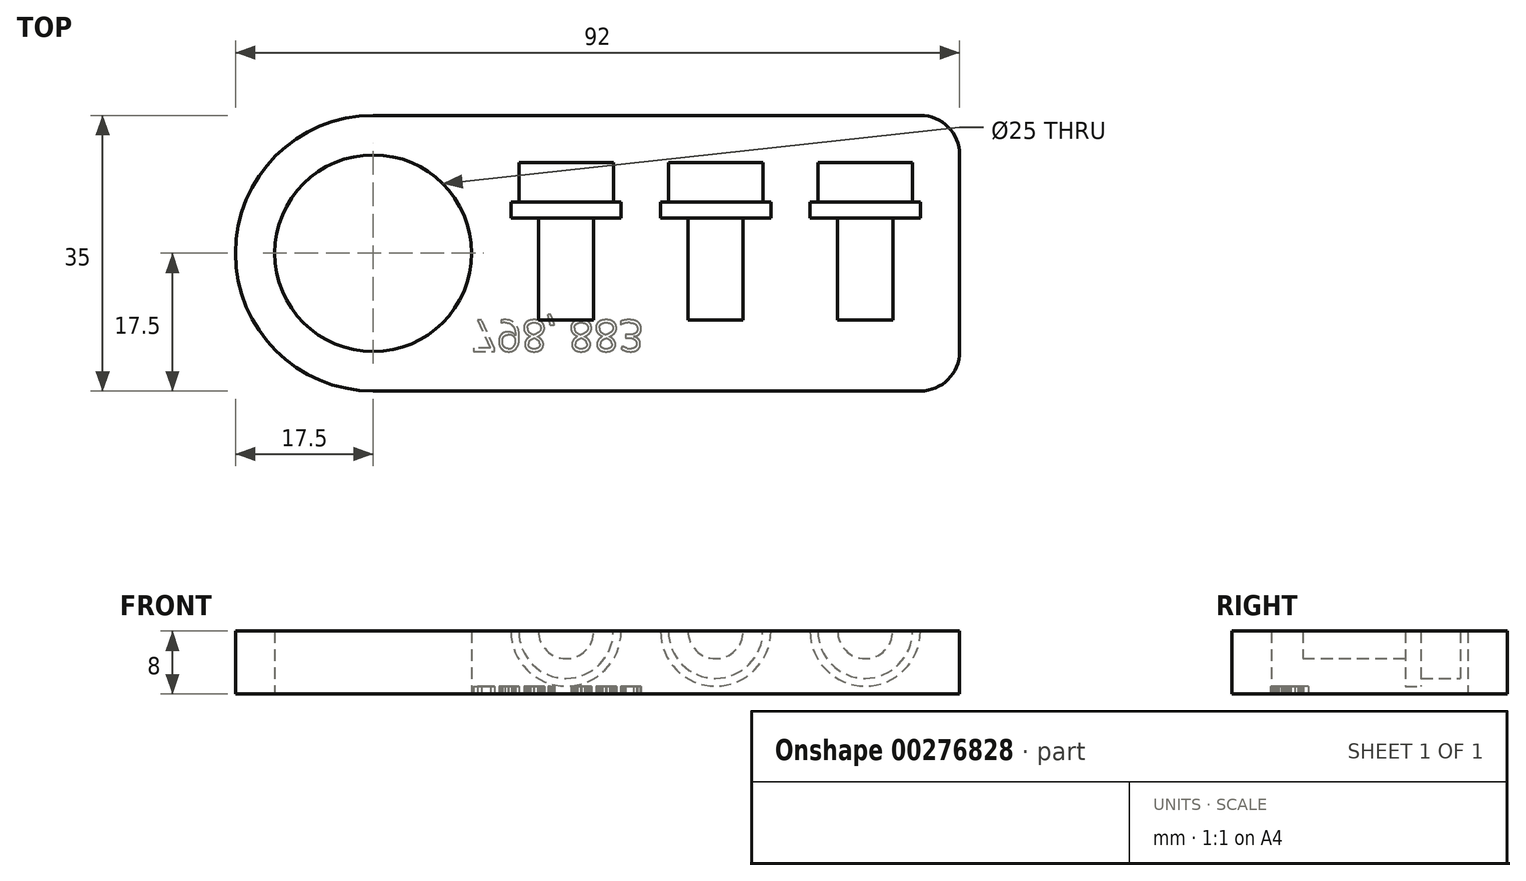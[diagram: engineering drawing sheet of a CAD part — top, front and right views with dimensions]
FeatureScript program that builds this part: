
annotation { "Feature Type Name" : "Feature", "Feature Type Description" : "" }
export const myFeature = defineFeature(function(context is Context, id is Id, definition is map)
    precondition{}
    {
        {
            var Q0;
            Q0=qCreatedBy(makeId("Top.planeOp"),FACE);
            var sketch = newSketch(context, id + "F0", { "sketchPlane" : qUnion([Q0])});
            skLineSegment(sketch, "E0.bottom", {"start": v(17.5, 0) * mm, "end": v(87, 0) * mm});
            skLineSegment(sketch, "E0.top", {"start": v(17.5, 35) * mm, "end": v(87, 35) * mm});
            skLineSegment(sketch, "E0.left", {"start": v(0, 17.5) * mm, "end": v(0, 17.5) * mm});
            skLineSegment(sketch, "E0.right", {"start": v(92, 5) * mm, "end": v(92, 30) * mm});
            skLineSegment(sketch, "E1.bottom", {"start": v(0, 0) * mm, "end": v(17.5, 0) * mm, "construction": true});
            skLineSegment(sketch, "E1.top", {"start": v(0, 17.5) * mm, "end": v(17.5, 17.5) * mm, "construction": true});
            skLineSegment(sketch, "E1.left", {"start": v(0, 0) * mm, "end": v(0, 17.5) * mm, "construction": true});
            skLineSegment(sketch, "E1.right", {"start": v(17.5, 0) * mm, "end": v(17.5, 17.5) * mm, "construction": true});
            skCircle(sketch, "E2", {"center": v(17.5, 17.5) * mm, "radius": 12.5 * mm});
            skPoint(sketch, "E3.visualSharp", {"position": v(0, 0) * mm});
            skArc(sketch, "E3.filletArc", {"start": v(0, 17.5) * mm, "mid": v(5.13, 5.13) * mm, "end": v(17.5, 0) * mm});
            skPoint(sketch, "E4.visualSharp", {"position": v(0, 35) * mm});
            skArc(sketch, "E4.filletArc", {"start": v(17.5, 35) * mm, "mid": v(5.13, 29.87) * mm, "end": v(0, 17.5) * mm});
            skPoint(sketch, "E5.visualSharp", {"position": v(92, 35) * mm});
            skArc(sketch, "E5.filletArc", {"start": v(92, 30) * mm, "mid": v(90.54, 33.54) * mm, "end": v(87, 35) * mm});
            skPoint(sketch, "E6.visualSharp", {"position": v(92, 0) * mm});
            skArc(sketch, "E6.filletArc", {"start": v(87, 0) * mm, "mid": v(90.54, 1.46) * mm, "end": v(92, 5) * mm});
            skSolve(sketch);
        }
        {
            var Q0;
            Q0=makeQuery(id+"F0.imprint","IMPRINT",FACE,{"disambiguationData":[TD([[makeQuery(id+"F0.imprint","IMPRINT",EDGE,{"derivedFrom":sQuery(id+"F0.wireOp",EDGE,"E0.bottom")}),1.0]])]});
            extrude(context, id + "F1", {"entities" : qUnion([Q0]), "depth" : 8 * mm});
        }
        {
            var Q0;
            Q0=makeQuery(id+"F1.opExtrude","CAP_FACE",FACE,{"disambiguationData":[OSD([sQuery(id+"F0.wireOp",EDGE,"E0.bottom"),sQuery(id+"F0.wireOp",EDGE,"E0.top"),sQuery(id+"F0.wireOp",EDGE,"E0.right"),sQuery(id+"F0.wireOp",EDGE,"E2"),sQuery(id+"F0.wireOp",EDGE,"E3.filletArc"),sQuery(id+"F0.wireOp",EDGE,"E4.filletArc"),sQuery(id+"F0.wireOp",EDGE,"E5.filletArc"),sQuery(id+"F0.wireOp",EDGE,"E6.filletArc")])],"isStart":false});
            var sketch = newSketch(context, id + "F2", { "sketchPlane" : qUnion([Q0])});
            skLineSegment(sketch, "E7.bottom", {"start": v(0, 0) * mm, "end": v(42, 0) * mm, "construction": true});
            skLineSegment(sketch, "E7.top", {"start": v(0, 9) * mm, "end": v(42, 9) * mm, "construction": true});
            skLineSegment(sketch, "E7.left", {"start": v(0, 0) * mm, "end": v(0, 9) * mm, "construction": true});
            skLineSegment(sketch, "E7.right", {"start": v(42, 0) * mm, "end": v(42, 9) * mm, "construction": true});
            skLineSegment(sketch, "E8", {"start": v(42, 9) * mm, "end": v(61, 9) * mm, "construction": true});
            skLineSegment(sketch, "E9", {"start": v(61, 9) * mm, "end": v(80, 9) * mm, "construction": true});
            skLineSegment(sketch, "E10.bottom", {"start": v(42, 9) * mm, "end": v(45.5, 9) * mm});
            skLineSegment(sketch, "E10.left", {"start": v(42, 9) * mm, "end": v(42, 22) * mm});
            skLineSegment(sketch, "E10.right", {"start": v(45.5, 9) * mm, "end": v(45.5, 22) * mm});
            skLineSegment(sketch, "E11.bottom", {"start": v(61, 9) * mm, "end": v(64.5, 9) * mm});
            skLineSegment(sketch, "E11.left", {"start": v(61, 9) * mm, "end": v(61, 22) * mm});
            skLineSegment(sketch, "E11.right", {"start": v(64.5, 9) * mm, "end": v(64.5, 22) * mm});
            skLineSegment(sketch, "E12.bottom", {"start": v(80, 9) * mm, "end": v(83.5, 9) * mm});
            skLineSegment(sketch, "E12.left", {"start": v(80, 9) * mm, "end": v(80, 22) * mm});
            skLineSegment(sketch, "E12.right", {"start": v(83.5, 9) * mm, "end": v(83.5, 22) * mm});
            skLineSegment(sketch, "E13.top", {"start": v(48, 24) * mm, "end": v(49, 24) * mm});
            skLineSegment(sketch, "E13.left", {"start": v(42, 22) * mm, "end": v(42, 24) * mm});
            skLineSegment(sketch, "E13.right", {"start": v(49, 22) * mm, "end": v(49, 24) * mm});
            skLineSegment(sketch, "E14.bottom", {"start": v(64.5, 22) * mm, "end": v(68, 22) * mm});
            skLineSegment(sketch, "E14.left", {"start": v(61, 22) * mm, "end": v(61, 24) * mm});
            skLineSegment(sketch, "E14.right", {"start": v(68, 22) * mm, "end": v(68, 24) * mm});
            skLineSegment(sketch, "E15.bottom", {"start": v(83.5, 22) * mm, "end": v(87, 22) * mm});
            skLineSegment(sketch, "E15.left", {"start": v(80, 22) * mm, "end": v(80, 24) * mm});
            skLineSegment(sketch, "E15.right", {"start": v(87, 22) * mm, "end": v(87, 24) * mm});
            skLineSegment(sketch, "E16.top", {"start": v(80, 29) * mm, "end": v(86, 29) * mm});
            skLineSegment(sketch, "E16.left", {"start": v(80, 24) * mm, "end": v(80, 29) * mm});
            skLineSegment(sketch, "E16.right", {"start": v(86, 24) * mm, "end": v(86, 29) * mm});
            skLineSegment(sketch, "E17.top", {"start": v(61, 29) * mm, "end": v(67, 29) * mm});
            skLineSegment(sketch, "E17.left", {"start": v(61, 24) * mm, "end": v(61, 29) * mm});
            skLineSegment(sketch, "E17.right", {"start": v(67, 24) * mm, "end": v(67, 29) * mm});
            skLineSegment(sketch, "E18.top", {"start": v(42, 29) * mm, "end": v(48, 29) * mm});
            skLineSegment(sketch, "E18.left", {"start": v(42, 24) * mm, "end": v(42, 29) * mm});
            skLineSegment(sketch, "E18.right", {"start": v(48, 24) * mm, "end": v(48, 29) * mm});
            skLineSegment(sketch, "E19", {"start": v(87, 24) * mm, "end": v(86, 24) * mm});
            skLineSegment(sketch, "E20", {"start": v(68, 24) * mm, "end": v(67, 24) * mm});
            skLineSegment(sketch, "E21", {"start": v(49, 22) * mm, "end": v(45.5, 22) * mm});
            skSolve(sketch);
        }
        {
            var Q0;
            Q0=makeQuery(id+"F2.imprint","IMPRINT",FACE,{"disambiguationData":[TD([[makeQuery(id+"F2.imprint","IMPRINT",EDGE,{"derivedFrom":sQuery(id+"F2.wireOp",EDGE,"E10.bottom")}),1.0]])]});
            var Q1;
            Q1=sQuery(id+"F2.wireOp",EDGE,"E10.left");
            revolve(context, id + "F3", {"operationType" : NewBodyOperationType.REMOVE, "entities" : qUnion([Q0]), "axis" : qUnion([Q1]), "revolveType" : RevolveType.FULL, "oppositeDirection" : true});
        }
        {
            var Q0;
            Q0=makeQuery(id+"F2.imprint","IMPRINT",FACE,{"disambiguationData":[TD([[makeQuery(id+"F2.imprint","IMPRINT",EDGE,{"derivedFrom":sQuery(id+"F2.wireOp",EDGE,"E11.bottom")}),1.0]])]});
            var Q1;
            Q1=sQuery(id+"F2.wireOp",EDGE,"E11.left");
            revolve(context, id + "F4", {"operationType" : NewBodyOperationType.REMOVE, "entities" : qUnion([Q0]), "axis" : qUnion([Q1]), "revolveType" : RevolveType.FULL, "oppositeDirection" : true});
        }
        {
            var Q0;
            Q0=makeQuery(id+"F2.imprint","IMPRINT",FACE,{"disambiguationData":[TD([[makeQuery(id+"F2.imprint","IMPRINT",EDGE,{"derivedFrom":sQuery(id+"F2.wireOp",EDGE,"E12.bottom")}),1.0]])]});
            var Q1;
            Q1=sQuery(id+"F2.wireOp",EDGE,"E12.left");
            revolve(context, id + "F5", {"operationType" : NewBodyOperationType.REMOVE, "entities" : qUnion([Q0]), "axis" : qUnion([Q1]), "revolveType" : RevolveType.FULL, "oppositeDirection" : true});
        }
        {
            var Q0;
            Q0=makeQuery(id+"F1.opExtrude","CAP_FACE",FACE,{"disambiguationData":[OSD([sQuery(id+"F0.wireOp",EDGE,"E0.bottom"),sQuery(id+"F0.wireOp",EDGE,"E0.top"),sQuery(id+"F0.wireOp",EDGE,"E0.right"),sQuery(id+"F0.wireOp",EDGE,"E2"),sQuery(id+"F0.wireOp",EDGE,"E3.filletArc"),sQuery(id+"F0.wireOp",EDGE,"E4.filletArc"),sQuery(id+"F0.wireOp",EDGE,"E5.filletArc"),sQuery(id+"F0.wireOp",EDGE,"E6.filletArc")])],"isStart":true});
            var sketch = newSketch(context, id + "F6", { "sketchPlane" : qUnion([Q0])});
            skLineSegment(sketch, "E22.bottom", {"start": v(0, 0) * mm, "end": v(30, 0) * mm, "construction": true});
            skLineSegment(sketch, "E22.top", {"start": v(0, -5) * mm, "end": v(30, -5) * mm, "construction": true});
            skLineSegment(sketch, "E22.left", {"start": v(0, 0) * mm, "end": v(0, -5) * mm, "construction": true});
            skLineSegment(sketch, "E22.right", {"start": v(30, 0) * mm, "end": v(30, -5) * mm, "construction": true});
            skText(sketch, "E23", { "text": "798, 883", "fontName": "OpenSans-Regular.ttf"});
            const initialGuessF6  = {"E23": [0.03, -0.009, 1, 0, 0.004]};
            skSetInitialGuess(sketch, initialGuessF6);
            skSolve(sketch);
        }
        {
            var Q0;
            Q0 = qSketchRegion(id + "F6", true);
            extrude(context, id + "F7", {"entities" : qUnion([Q0]), "operationType" : NewBodyOperationType.REMOVE, "oppositeDirection" : true, "depth" : 1 * mm});
        }
    });
